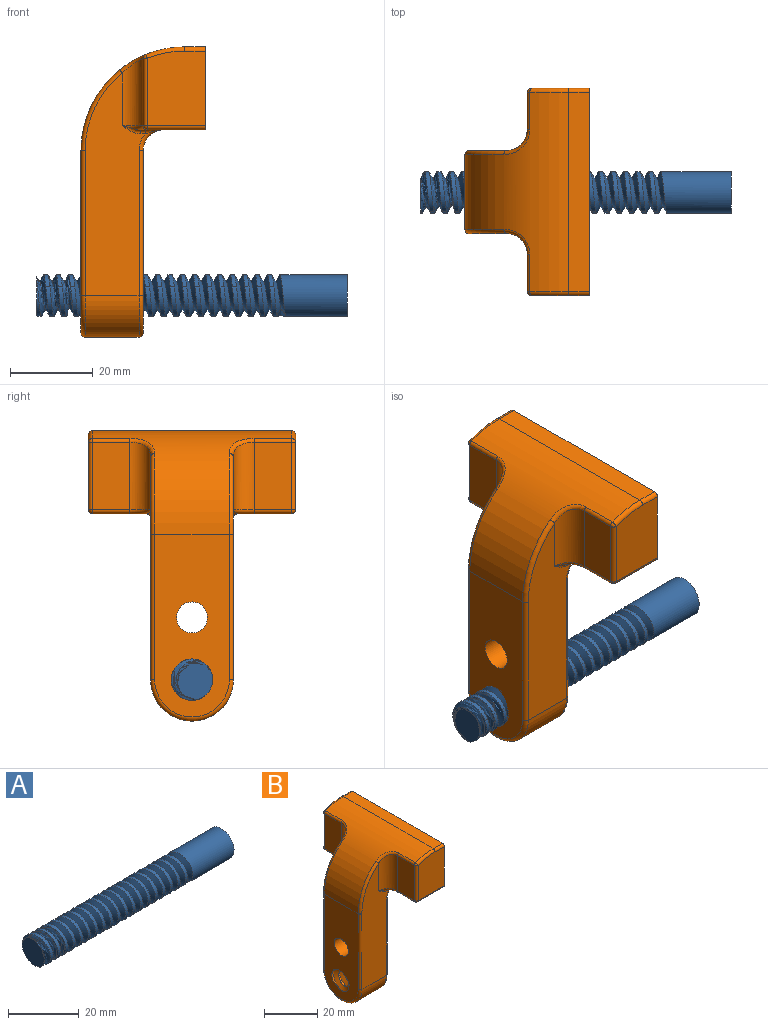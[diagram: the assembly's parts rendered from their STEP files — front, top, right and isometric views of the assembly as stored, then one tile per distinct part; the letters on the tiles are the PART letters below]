
ASSEMBLY  parts=2 mates=1
PART A: 27 faces, bbox 76.9x10.9x12.5 mm
  f0: cylinder r=5mm len=18.75mm, axis (1,0,0), area 521.9mm2, adj f19,f22,f23,f24,f25,f26
  f1: cylinder r=5mm len=10mm, axis (1,0,0), area 28.5mm2, adj f2,f20,f21,f23,f24
  f2: cylinder r=5mm len=10mm, axis (1,0,0), area 31.4mm2, adj f1,f3,f23,f24
  f3: cylinder r=5mm len=10mm, axis (1,0,0), area 31.4mm2, adj f2,f4,f23,f24
  f4: cylinder r=5mm len=10mm, axis (1,0,0), area 31.4mm2, adj f3,f5,f23,f24
  f5: cylinder r=5mm len=10mm, axis (1,0,0), area 31.4mm2, adj f4,f6,f23,f24
  f6: cylinder r=5mm len=10mm, axis (1,0,0), area 31.4mm2, adj f5,f7,f23,f24
  f7: cylinder r=5mm len=10mm, axis (1,0,0), area 31.4mm2, adj f6,f8,f23,f24
  f8: cylinder r=5mm len=10mm, axis (1,0,0), area 31.4mm2, adj f7,f9,f23,f24
  f9: cylinder r=5mm len=10mm, axis (1,0,0), area 31.4mm2, adj f8,f10,f23,f24
  f10: cylinder r=5mm len=10mm, axis (1,0,0), area 31.4mm2, adj f9,f11,f23,f24
  f11: cylinder r=5mm len=10mm, axis (1,0,0), area 31.4mm2, adj f10,f12,f23,f24
  f12: cylinder r=5mm len=10mm, axis (1,0,0), area 31.4mm2, adj f11,f13,f23,f24
  f13: cylinder r=5mm len=10mm, axis (1,0,0), area 31.4mm2, adj f12,f14,f23,f24
  f14: cylinder r=5mm len=10mm, axis (1,0,0), area 31.4mm2, adj f13,f15,f23,f24
  f15: cylinder r=5mm len=10mm, axis (1,0,0), area 31.4mm2, adj f14,f16,f23,f24
  f16: cylinder r=5mm len=10mm, axis (1,0,0), area 31.4mm2, adj f15,f17,f23,f24
  f17: cylinder r=5mm len=10mm, axis (1,0,0), area 31.4mm2, adj f16,f18,f23,f24
  f18: cylinder r=5mm len=10mm, axis (1,0,0), area 31.4mm2, adj f17,f19,f23,f24
  f19: cylinder r=5mm len=10mm, axis (1,0,0), area 31.4mm2, adj f0,f18,f23,f24
  f20: cylinder r=5mm len=2.5mm, axis (1,0,0), area 0.3mm2, adj f1,f21,f24
  f21: plane 10.13x9.72mm, normal (-1,0,0), area 62.5mm2, adj f1,f20,f23,f24
  f22: plane 10x10mm, normal (1,0,0), area 78.5mm2, adj f0
  f23: bspline ~61x11.55mm, area 1036.3mm2, adj f0,f1,f2,f3,f4,f5,f6,f7
  f24: bspline ~60x11.55mm, area 1005.8mm2, adj f0,f1,f2,f3,f4,f5,f6,f7
  f25: plane 4.26x2.21mm, normal (-0.87,0.5,0), area 5.3mm2, adj f0,f23,f26
  f26: plane 4.26x2.21mm, normal (0.87,0.5,0), area 5.3mm2, adj f0,f24,f25
PART B: 56 faces, bbox 32.4x50.4x71.6 mm
  f0: plane 44x18mm, normal (-1,0,0), area 650.6mm2, adj f2,f3,f4,f16,f17,f42,f44,f47
  f1: plane 44x18mm, normal (1,0,0), area 650.6mm2, adj f2,f3,f8,f16,f17,f27,f30,f33
  f2: bspline ~17.5x11.55mm, area 260.9mm2, adj f0,f1,f3,f17
  f3: bspline ~17x11.55mm, area 260.9mm2, adj f0,f1,f2,f17
  f4: cylinder r=25mm len=48mm, axis (0,1,0), area 1013mm2, adj f0,f10,f32,f36,f38,f40,f50,f51
  f5: plane 18x14mm, normal (0,-1,0), area 246.8mm2, adj f9,f45,f48,f51,f52
  f6: plane 18x14mm, normal (0,1,0), area 246.8mm2, adj f9,f26,f29,f31,f32
  f7: plane 48.35x15.88mm, normal (0,0,-1), area 594.4mm2, adj f8,f9,f20,f22,f23,f25,f26,f37
  f8: cylinder r=5mm len=18mm, axis (0,1,0), area 141.4mm2, adj f1,f7,f24,f35
  f9: plane 50x20mm, normal (1,0,0), area 999.1mm2, adj f5,f6,f7,f10,f26,f29,f45,f48
  f10: plane 48x5mm, normal (0,0,1), area 240mm2, adj f4,f9,f29,f48
  f11: plane 54.09x14.88mm, normal (0,-1,0), area 593.6mm2, adj f15,f19,f33,f35,f39,f41,f47,f50
  f12: plane 54.09x14.88mm, normal (0,1,0), area 593.6mm2, adj f15,f18,f20,f21,f24,f27,f40,f42
  f13: plane 16.25x9mm, normal (-1,0,0), area 146.2mm2, adj f18,f25,f31,f36
  f14: plane 16.25x9mm, normal (-1,0,0), area 146.2mm2, adj f19,f46,f52,f55
  f15: cylinder r=10mm len=20mm, axis (1,0,0), area 408.4mm2, adj f11,f12,f30,f44
  f16: cylinder r=3.75mm len=15mm, axis (-1,0,0), area 353.4mm2, adj f0,f1
  f17: cylinder r=5mm len=15mm, axis (-1,0,0), area 157.3mm2, adj f0,f1,f2,f3
  f18: cylinder r=5mm len=16.25mm, axis (0,0,-1), area 118.8mm2, adj f12,f13,f23,f38
  f19: cylinder r=5mm len=16.25mm, axis (0,0,-1), area 118.8mm2, adj f11,f14,f43,f53
  f20: cylinder r=1mm len=1.06mm, axis (-1,0,0), area 1.7mm2, adj f7,f12,f21,f22
  f21: bspline ~5.15x2mm, area 3.2mm2, adj f12,f20,f23
  f22: bspline ~5.15x2mm, area 3.2mm2, adj f7,f20,f24
  f23: torus R=6mm, axis (0,0,1), area 9.1mm2, adj f7,f18,f21,f25
  f24: torus R=6mm, axis (0,-1,0), area 9.1mm2, adj f8,f12,f22,f27
  f25: cylinder r=1mm len=9mm, axis (0,1,0), area 14.1mm2, adj f7,f13,f23,f28
  f26: cylinder r=1mm len=14mm, axis (1,0,0), area 22mm2, adj f6,f7,f9,f28
  f27: cylinder r=1mm len=35mm, axis (0,0,1), area 55mm2, adj f1,f12,f24,f30
  f28: sphere r=1mm, area 1.6mm2, adj f25,f26,f31
  f29: cylinder r=1mm len=5mm, axis (-1,0,0), area 7.9mm2, adj f6,f9,f10,f32
  f30: torus R=9mm, axis (-1,0,0), area 47.6mm2, adj f1,f15,f27,f33
  f31: cylinder r=1mm len=16.25mm, axis (0,0,1), area 25.5mm2, adj f6,f13,f28,f34
  f32: torus R=24mm, axis (0,-1,0), area 14.9mm2, adj f4,f6,f29,f34
  f33: cylinder r=1mm len=35mm, axis (0,0,-1), area 55mm2, adj f1,f11,f30,f35
  f34: sphere r=1mm, area 1.2mm2, adj f31,f32,f36
  f35: torus R=6mm, axis (0,-1,0), area 9.1mm2, adj f8,f11,f33,f37
  f36: cylinder r=1mm len=9mm, axis (0,1,0), area 10.7mm2, adj f4,f13,f34,f38
  f37: bspline ~5.15x2mm, area 3.2mm2, adj f7,f35,f39
  f38: bspline ~7.25x7.06mm, area 12.5mm2, adj f4,f18,f36,f40
  f39: cylinder r=1mm len=1.06mm, axis (1,0,0), area 1.7mm2, adj f7,f11,f37,f41
  f40: torus R=24mm, axis (0,-1,0), area 34.7mm2, adj f4,f12,f38,f42
  f41: bspline ~5.15x2mm, area 3.2mm2, adj f11,f39,f43
  f42: cylinder r=1mm len=35mm, axis (0,0,-1), area 55mm2, adj f0,f12,f40,f44
  f43: torus R=6mm, axis (0,0,1), area 9.1mm2, adj f7,f19,f41,f46
  f44: torus R=9mm, axis (-1,0,0), area 47.6mm2, adj f0,f15,f42,f47
  f45: cylinder r=1mm len=14mm, axis (-1,0,0), area 22mm2, adj f5,f7,f9,f49
  f46: cylinder r=1mm len=9mm, axis (0,1,0), area 14.1mm2, adj f7,f14,f43,f49
  f47: cylinder r=1mm len=35mm, axis (0,0,1), area 55mm2, adj f0,f11,f44,f50
  f48: cylinder r=1mm len=5mm, axis (1,0,0), area 7.9mm2, adj f5,f9,f10,f51
  f49: sphere r=1mm, area 1.6mm2, adj f45,f46,f52
  f50: torus R=24mm, axis (0,-1,0), area 34.7mm2, adj f4,f11,f47,f53
  f51: torus R=24mm, axis (0,-1,0), area 14.9mm2, adj f4,f5,f48,f54
  f52: cylinder r=1mm len=16.25mm, axis (0,0,1), area 25.5mm2, adj f5,f14,f49,f54
  f53: bspline ~7.25x7.06mm, area 12.5mm2, adj f4,f19,f50,f55
  f54: sphere r=1mm, area 1.2mm2, adj f51,f52,f55
  f55: cylinder r=1mm len=9mm, axis (0,1,0), area 10.7mm2, adj f4,f14,f53,f54
PLACE A rot(axis=(-1,0,0),114.8deg) t=(9.28,-9.08,14.19)mm
PLACE B at identity fixed
MATE cylindrical A.f0 <-> B.f15  axis (-1,0,0) through (-65.72,0,10)mm
